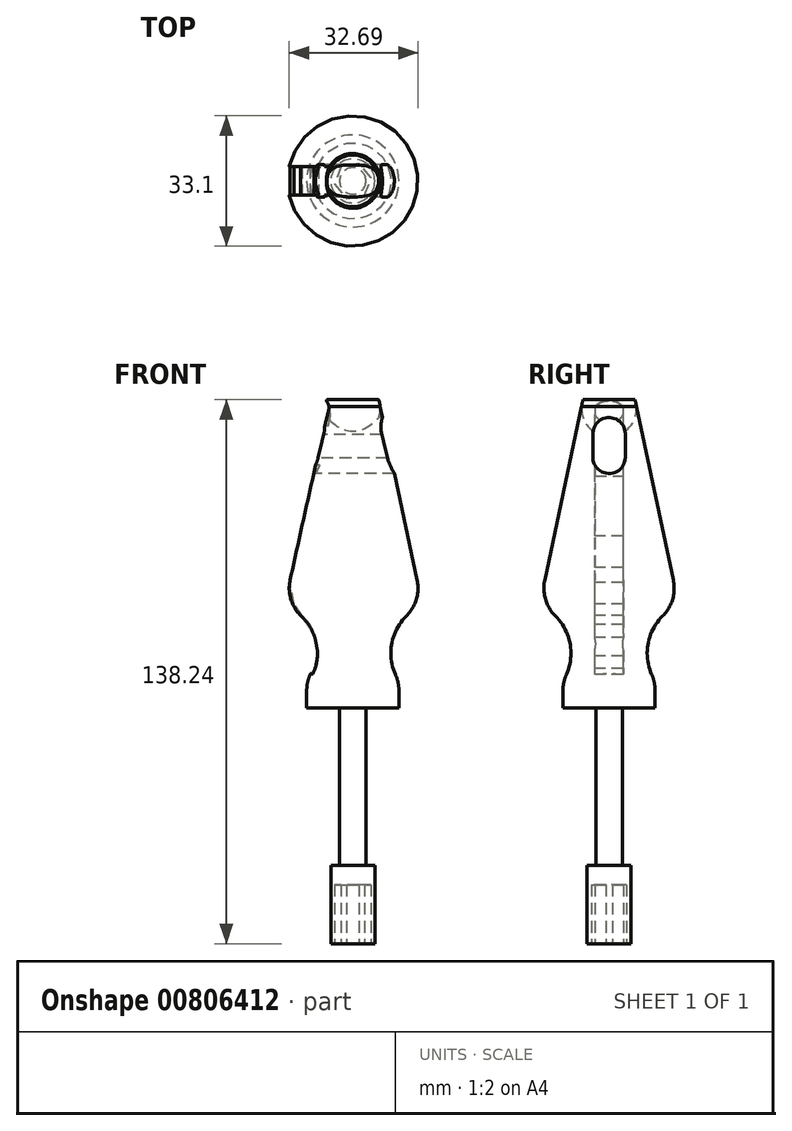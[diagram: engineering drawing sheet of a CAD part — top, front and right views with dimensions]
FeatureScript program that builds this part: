
annotation { "Feature Type Name" : "Feature", "Feature Type Description" : "" }
export const myFeature = defineFeature(function(context is Context, id is Id, definition is map)
    precondition{}
    {
        {
            var Q0;
            Q0=qCreatedBy(makeId("Right.planeOp"),FACE);
            var sketch = newSketch(context, id + "F0", { "sketchPlane" : qUnion([Q0])});
            skCircle(sketch, "E0", {"center": v(0, 59.79) * mm, "radius": 6.98 * mm});
            skLineSegment(sketch, "E1", {"start": v(-6.57, 62.13) * mm, "end": v(-17.7, 9.89) * mm});
            skArc(sketch, "E2", {"start": v(-11.7, -9.34) * mm, "mid": v(-10.28, 1.65) * mm, "end": v(-17.7, 9.89) * mm});
            skLineSegment(sketch, "E3", {"start": v(-11.7, -9.34) * mm, "end": v(-11.7, -16.24) * mm});
            skLineSegment(sketch, "E4", {"start": v(-11.7, -16.24) * mm, "end": v(0, -16.24) * mm});
            skLineSegment(sketch, "E5", {"start": v(0, -16.24) * mm, "end": v(0, 66.77) * mm});
            skLineSegment(sketch, "E6", {"start": v(-3.36, -16.24) * mm, "end": v(-3.36, -56.16) * mm});
            skLineSegment(sketch, "E7", {"start": v(-3.36, -56.16) * mm, "end": v(-5.59, -56.16) * mm});
            skLineSegment(sketch, "E8", {"start": v(-5.59, -56.16) * mm, "end": v(-5.59, -76.1) * mm});
            skLineSegment(sketch, "E9", {"start": v(-5.59, -76.1) * mm, "end": v(0, -76.1) * mm});
            skLineSegment(sketch, "E10", {"start": v(0, -76.1) * mm, "end": v(0, -16.24) * mm});
            skSolve(sketch);
        }
        {
            var Q0;
            Q0=qCreatedBy(makeId("Right.planeOp"),FACE);
            var sketch = newSketch(context, id + "F1", { "sketchPlane" : qUnion([Q0])});
            skLineSegment(sketch, "E11", {"start": v(0, 72.67) * mm, "end": v(0, -57.61) * mm});
            skSolve(sketch);
        }
        {
            var Q0;
            {var subQ0=sQuery(id+"F0.wireOp",EDGE,"E2");Q0=makeQuery(id+"F0.imprint","IMPRINT",FACE,{"disambiguationData":[TD([[makeQuery(id+"F0.imprint","IMPRINT",EDGE,{"derivedFrom":subQ0}),-1.0]])]});}
            var Q1;
            {var subQ0=sQuery(id+"F0.wireOp",EDGE,"E1");var subQ1=sQuery(id+"F0.wireOp",EDGE,"E0");var subQ2=makeQuery(id+"F0.imprint","INTERSECT",VERTEX,{"disambiguationData":[OD(0.0)],"derivedFrom":[subQ1,subQ0]});Q1=makeQuery(id+"F0.imprint","IMPRINT",FACE,{"disambiguationData":[TD([[makeQuery(id+"F0.imprint","IMPRINT",EDGE,{"disambiguationData":[TD([[subQ2,1.0]])],"derivedFrom":subQ1}),1.0]])]});}
            var Q2;
            {var subQ0=sQuery(id+"F0.wireOp",EDGE,"E6");Q2=makeQuery(id+"F0.imprint","IMPRINT",FACE,{"disambiguationData":[TD([[makeQuery(id+"F0.imprint","IMPRINT",EDGE,{"derivedFrom":subQ0}),1.0]])]});}
            var Q3;
            Q3=sQuery(id+"F0.wireOp",EDGE,"E5");
            revolve(context, id + "F2", {"surfaceOperationType" : NewSurfaceOperationType.NEW, "entities" : qUnion([Q0, Q1, Q2]), "axis" : qUnion([Q3]), "revolveType" : RevolveType.FULL});
        }
        {
            var Q0;
            Q0=qCreatedBy(makeId("Right.planeOp"),FACE);
            var sketch = newSketch(context, id + "F3", { "sketchPlane" : qUnion([Q0])});
            skArc(sketch, "E12", {"start": v(4.11, 53.46) * mm, "mid": v(-0.11, 57.57) * mm, "end": v(-4.1, 53.24) * mm});
            skLineSegment(sketch, "E13", {"start": v(4.11, 53.46) * mm, "end": v(4.11, 47.46) * mm});
            skLineSegment(sketch, "E14", {"start": v(-4.1, 53.24) * mm, "end": v(-4.1, 47.24) * mm});
            skArc(sketch, "E15", {"start": v(-4.1, 47.24) * mm, "mid": v(0.11, 43.35) * mm, "end": v(4.11, 47.46) * mm});
            skSolve(sketch);
        }
        {
            var Q0;
            Q0 = qSketchRegion(id + "F3", true);
            extrude(context, id + "F4", {"entities" : qUnion([Q0]), "operationType" : NewBodyOperationType.REMOVE, "endBound" : BoundingType.SYMMETRIC, "depth" : 25 * mm, "offsetDistance" : 25 * mm});
        }
        {
            var Q0;
            Q0=makeQuery(id+"F2.opRevolve","SWEPT_FACE",FACE,{"disambiguationData":[OSD([sQuery(id+"F0.wireOp",EDGE,"E2")])]});
            fillet(context, id + "F5", {"entities" : qUnion([Q0]), "radius" : 10 * mm, "tangentPropagation" : true, "allowEdgeOverflow" : false});
        }
        {
            var Q0;
            Q0=qCreatedBy(makeId("Top.planeOp"),FACE);
            cPlane(context, id + "F6", {"entities" : qUnion([Q0]), "cplaneType" : CPlaneType.OFFSET, "offset" : 25 * mm, "width" : 150 * mm, "height" : 150 * mm});
        }
        {
            var Q0;
            Q0=qCreatedBy(id+"F6.planeOp",FACE);
            var sketch = newSketch(context, id + "F7", { "sketchPlane" : qUnion([Q0])});
            skLineSegment(sketch, "E16.bottom", {"start": v(-13.75, 3.64) * mm, "end": v(-15.77, 3.64) * mm});
            skLineSegment(sketch, "E16.top", {"start": v(-13.75, -3.64) * mm, "end": v(-15.77, -3.64) * mm});
            skLineSegment(sketch, "E16.left", {"start": v(-13.75, 3.64) * mm, "end": v(-13.75, -3.64) * mm});
            skLineSegment(sketch, "E16.right", {"start": v(-15.77, 3.64) * mm, "end": v(-15.77, -3.64) * mm});
            skPoint(sketch, "E16.middle", {"position": v(-14.76, 0) * mm});
            skSolve(sketch);
        }
        {
            var Q0;
            Q0=qCreatedBy(makeId("Front.planeOp"),FACE);
            var sketch = newSketch(context, id + "F8", { "sketchPlane" : qUnion([Q0])});
            skLineSegment(sketch, "E17", {"start": v(-10.8, -7.48) * mm, "end": v(-10.1, -5.9) * mm});
            skLineSegment(sketch, "E18", {"start": v(-10.1, -5.9) * mm, "end": v(-9.52, -2.94) * mm});
            skLineSegment(sketch, "E19", {"start": v(-9.52, -2.94) * mm, "end": v(-10.1, 0) * mm});
            skLineSegment(sketch, "E20", {"start": v(-10.1, 0) * mm, "end": v(-10.39, 1.48) * mm});
            skLineSegment(sketch, "E21", {"start": v(-10.39, 1.48) * mm, "end": v(-11.61, 4.55) * mm});
            skLineSegment(sketch, "E22", {"start": v(-11.61, 4.55) * mm, "end": v(-13.56, 6.78) * mm});
            skLineSegment(sketch, "E23", {"start": v(-13.56, 6.78) * mm, "end": v(-15.64, 9.87) * mm});
            skLineSegment(sketch, "E24", {"start": v(-15.64, 9.87) * mm, "end": v(-16.16, 12.5) * mm});
            skLineSegment(sketch, "E25", {"start": v(-16.16, 12.5) * mm, "end": v(-16.8, 15.75) * mm});
            skLineSegment(sketch, "E26", {"start": v(-16.8, 15.75) * mm, "end": v(-15.64, 19.67) * mm});
            skLineSegment(sketch, "E27", {"start": v(-15.64, 19.67) * mm, "end": v(-14.06, 27.44) * mm});
            skLineSegment(sketch, "E28", {"start": v(-14.06, 27.44) * mm, "end": v(-12.04, 36.66) * mm});
            skLineSegment(sketch, "E29", {"start": v(-12.04, 36.66) * mm, "end": v(-10.64, 43.09) * mm});
            skFitSpline(sketch, "E30", {"points": [v(-10.64, 43.09) * mm, v(-9.3, 45.45) * mm, v(-7.94, 51.14) * mm, v(-6.93, 55.82) * mm, v(-6.72, 59.92) * mm, v(-7.87, 62) * mm], "startDerivative": vector(8.43, 11.95) * mm, "endDerivative": vector(-9.08, 11.74) * mm});
            skSolve(sketch);
        }
        {
            var Q0;
            Q0=makeQuery(id+"F7.imprint","IMPRINT",FACE,{"disambiguationData":[TD([[makeQuery(id+"F7.imprint","IMPRINT",EDGE,{"derivedFrom":sQuery(id+"F7.wireOp",EDGE,"E16.bottom")}),1.0]])]});
            var Q1;
            Q1=sQuery(id+"F8.wireOp",EDGE,"E30");
            var Q2;
            Q2=sQuery(id+"F8.wireOp",EDGE,"E29");
            var Q3;
            Q3=sQuery(id+"F8.wireOp",EDGE,"E28");
            var Q4;
            Q4=sQuery(id+"F8.wireOp",EDGE,"E27");
            var Q5;
            Q5=sQuery(id+"F8.wireOp",EDGE,"E26");
            var Q6;
            Q6=sQuery(id+"F8.wireOp",EDGE,"E25");
            var Q7;
            Q7=sQuery(id+"F8.wireOp",EDGE,"E24");
            var Q8;
            Q8=sQuery(id+"F8.wireOp",EDGE,"E23");
            var Q9;
            Q9=sQuery(id+"F8.wireOp",EDGE,"E22");
            var Q10;
            Q10=sQuery(id+"F8.wireOp",EDGE,"E21");
            var Q11;
            Q11=sQuery(id+"F8.wireOp",EDGE,"E19");
            var Q12;
            Q12=sQuery(id+"F8.wireOp",EDGE,"E20");
            var Q13;
            Q13=sQuery(id+"F8.wireOp",EDGE,"E18");
            var Q14;
            Q14=sQuery(id+"F8.wireOp",EDGE,"E17");
            sweep(context, id + "F9", {"operationType" : NewBodyOperationType.REMOVE, "profiles" : qUnion([Q0]), "path" : qUnion([Q1, Q2, Q3, Q4, Q5, Q6, Q7, Q8, Q9, Q10, Q11, Q12, Q13, Q14])});
        }
        {
            var Q0;
            Q0=sQuery(id+"F1.wireOp",EDGE,"E11");
            var Q1;
            Q1=qCreatedBy(makeId("Front.planeOp"),FACE);
            cPlane(context, id + "F10", {"entities" : qUnion([Q0, Q1]), "cplaneType" : CPlaneType.LINE_ANGLE, "offset" : 25 * mm, "angle" : 30 * degree, "width" : 150 * mm, "height" : 150 * mm});
        }
        {
            var Q0;
            Q0=makeQuery(id+"F2.opRevolve","SWEPT_FACE",FACE,{"disambiguationData":[OSD([sQuery(id+"F0.wireOp",EDGE,"E9")])]});
            var sketch = newSketch(context, id + "F11", { "sketchPlane" : qUnion([Q0])});
            skCircle(sketch, "E31.cCircle", {"center": v(0, 0) * mm, "radius": 4.08 * mm, "construction": true});
            skLineSegment(sketch, "E31.0", {"start": v(4.65, -0.82) * mm, "end": v(1.61, -4.43) * mm});
            skLineSegment(sketch, "E31.1", {"start": v(1.61, -4.43) * mm, "end": v(-3.03, -3.61) * mm});
            skLineSegment(sketch, "E31.2", {"start": v(-3.03, -3.61) * mm, "end": v(-4.65, 0.82) * mm});
            skLineSegment(sketch, "E31.3", {"start": v(-4.65, 0.82) * mm, "end": v(-1.61, 4.43) * mm});
            skLineSegment(sketch, "E31.4", {"start": v(-1.61, 4.43) * mm, "end": v(3.03, 3.61) * mm});
            skLineSegment(sketch, "E31.5", {"start": v(3.03, 3.61) * mm, "end": v(4.65, -0.82) * mm});
            skPoint(sketch, "E31.0.midPoint", {"position": v(3.13, -2.63) * mm});
            skSolve(sketch);
        }
        {
            var Q0;
            Q0=makeQuery(id+"F11.imprint","IMPRINT",FACE,{"disambiguationData":[TD([[makeQuery(id+"F11.imprint","IMPRINT",EDGE,{"derivedFrom":sQuery(id+"F11.wireOp",EDGE,"E31.0")}),-1.0]])]});
            extrude(context, id + "F12", {"entities" : qUnion([Q0]), "operationType" : NewBodyOperationType.REMOVE, "oppositeDirection" : true, "depth" : 15 * mm, "offsetDistance" : 25 * mm});
        }
    });
